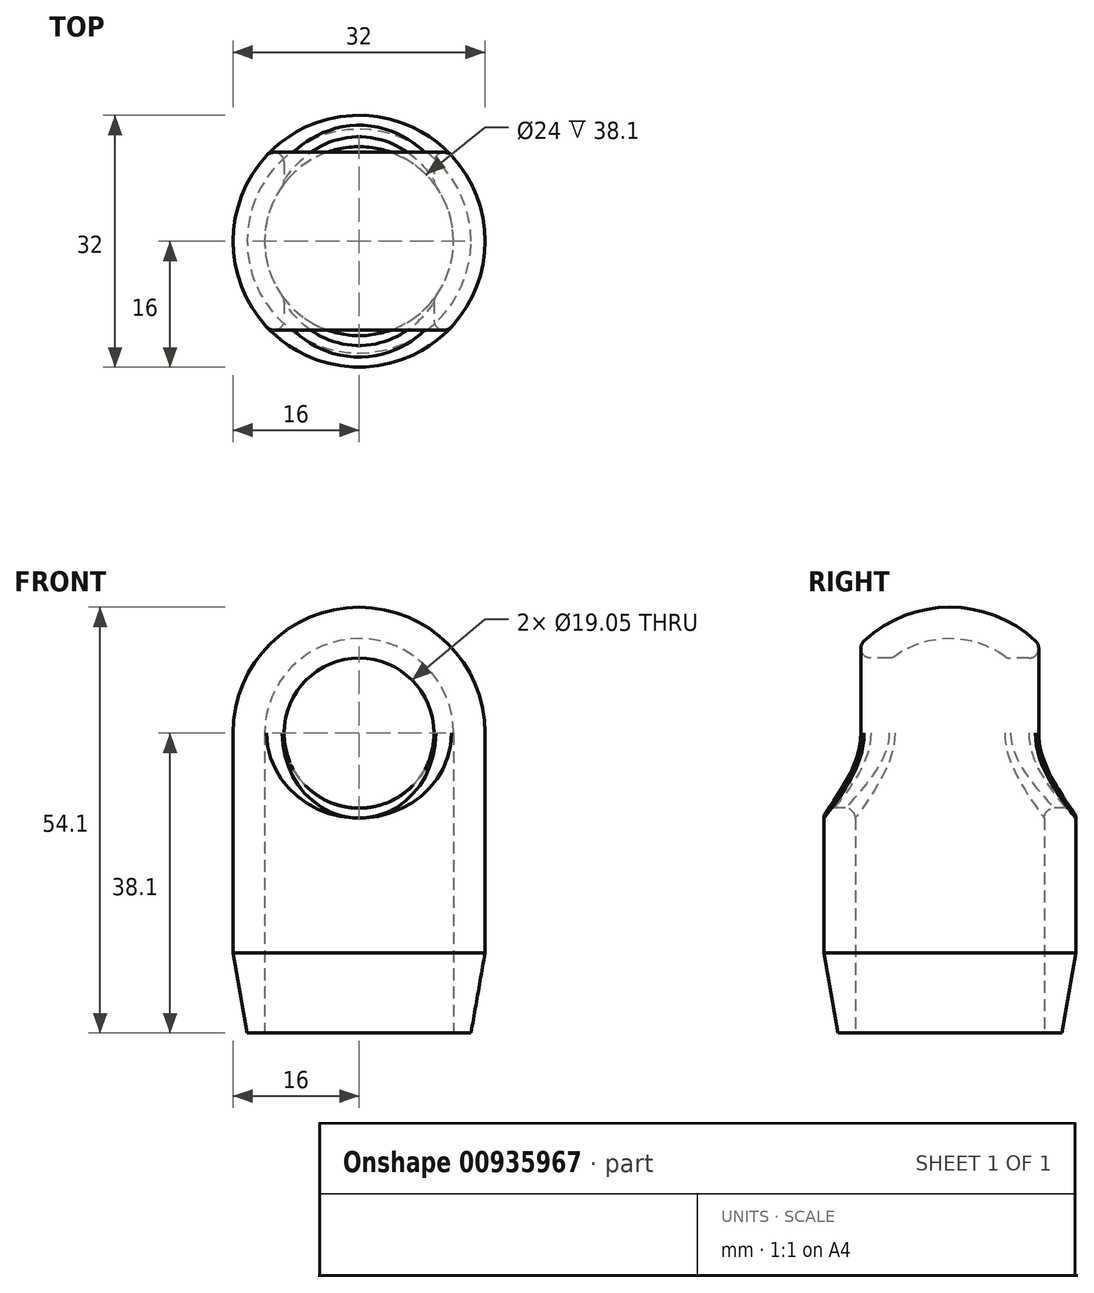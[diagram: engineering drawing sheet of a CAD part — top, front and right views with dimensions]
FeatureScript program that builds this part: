
annotation { "Feature Type Name" : "Feature", "Feature Type Description" : "" }
export const myFeature = defineFeature(function(context is Context, id is Id, definition is map)
    precondition{}
    {
        {
            var Q0;
            Q0=qCreatedBy(makeId("Top.planeOp"),FACE);
            var sketch = newSketch(context, id + "F0", { "sketchPlane" : qUnion([Q0])});
            skCircle(sketch, "E0", {"center": v(0, 0) * mm, "radius": 16 * mm});
            skCircle(sketch, "E1", {"center": v(0, 0) * mm, "radius": 12 * mm});
            skSolve(sketch);
        }
        {
            var Q0;
            Q0 = qSketchRegion(id + "F0", true);
            extrude(context, id + "F1", {"entities" : qUnion([Q0]), "depth" : 12.7 * mm, "offsetDistance" : 25.4 * mm, "hasSecondDirection" : true, "secondDirectionOppositeDirection" : true, "secondDirectionDepth" : 25.4 * mm});
        }
        {
            var Q0;
            Q0=makeQuery(id+"F1.opExtrude","CAP_FACE",FACE,{"disambiguationData":[OSD([sQuery(id+"F0.wireOp",EDGE,"E0"),sQuery(id+"F0.wireOp",EDGE,"E1")])],"isStart":false});
            var sketch = newSketch(context, id + "F2", { "sketchPlane" : qUnion([Q0])});
            skArc(sketch, "E2", {"start": v(0, -16) * mm, "mid": v(-16, 0) * mm, "end": v(0, 16) * mm});
            skLineSegment(sketch, "E3", {"start": v(0, 12) * mm, "end": v(0, -12) * mm, "construction": true});
            skArc(sketch, "E4", {"start": v(0, 12) * mm, "mid": v(-12, 0) * mm, "end": v(0, -12) * mm});
            skLineSegment(sketch, "E5", {"start": v(0, 16) * mm, "end": v(0, 12) * mm});
            skLineSegment(sketch, "E6", {"start": v(0, -12) * mm, "end": v(0, -16) * mm});
            skSolve(sketch);
        }
        {
            var Q0;
            Q0=makeQuery(id+"F2.imprint","IMPRINT",FACE,{"disambiguationData":[TD([[makeQuery(id+"F2.imprint","IMPRINT",EDGE,{"derivedFrom":sQuery(id+"F2.wireOp",EDGE,"E2")}),1.0]])]});
            var Q1;
            Q1=sQuery(id+"F2.wireOp",EDGE,"E2");
            var Q2;
            Q2=sQuery(id+"F2.wireOp",EDGE,"E3");
            revolve(context, id + "F3", {"operationType" : NewBodyOperationType.ADD, "surfaceOperationType" : NewSurfaceOperationType.ADD, "entities" : qUnion([Q0]), "surfaceEntities" : qUnion([Q1]), "axis" : qUnion([Q2]), "revolveType" : RevolveType.ONE_DIRECTION, "oppositeDirection" : true, "angle" : 180 * degree});
        }
        {
            var Q0;
            Q0=qCreatedBy(makeId("Front.planeOp"),FACE);
            var sketch = newSketch(context, id + "F4", { "sketchPlane" : qUnion([Q0])});
            skCircle(sketch, "E7", {"center": v(0, 12.7) * mm, "radius": 9.53 * mm});
            skSolve(sketch);
        }
        {
            var Q0;
            Q0 = qSketchRegion(id + "F4", true);
            extrude(context, id + "F5", {"entities" : qUnion([Q0]), "operationType" : NewBodyOperationType.REMOVE, "endBound" : BoundingType.THROUGH_ALL, "oppositeDirection" : true, "depth" : 25.4 * mm, "offsetDistance" : 25.4 * mm, "hasSecondDirection" : true, "secondDirectionBound" : SecondDirectionBoundingType.THROUGH_ALL, "secondDirectionOppositeDirection" : false, "secondDirectionDepth" : 25.4 * mm});
        }
        {
            var Q0;
            Q0=makeQuery(id+"F5.boolean.opBoolean","COPY",FACE,{"disambiguationData":[OD(0.0)],"derivedFrom":makeQuery(id+"F5.opExtrude","SWEPT_FACE",FACE,{"disambiguationData":[OSD([sQuery(id+"F4.wireOp",EDGE,"E7")])]})});
            var Q1;
            Q1=makeQuery(id+"F5.boolean.opBoolean","COPY",FACE,{"disambiguationData":[OD(1.0)],"derivedFrom":makeQuery(id+"F5.opExtrude","SWEPT_FACE",FACE,{"disambiguationData":[OSD([sQuery(id+"F4.wireOp",EDGE,"E7")])]})});
            fillet(context, id + "F6", {"entities" : qUnion([Q0, Q1]), "radius" : 1.27 * mm, "tangentPropagation" : true, "allowEdgeOverflow" : false});
        }
        {
            var Q0;
            Q0=makeQuery(id+"F1.opExtrude","CAP_EDGE",EDGE,{"disambiguationData":[OSD([sQuery(id+"F0.wireOp",EDGE,"E0")])],"isStart":true});
            chamfer(context, id + "F7", {"entities" : qUnion([Q0]), "chamferType" : ChamferType.OFFSET_ANGLE, "width" : 10.16 * mm, "oppositeDirection" : false, "angle" : 10 * degree, "tangentPropagation" : true});
        }
    });
